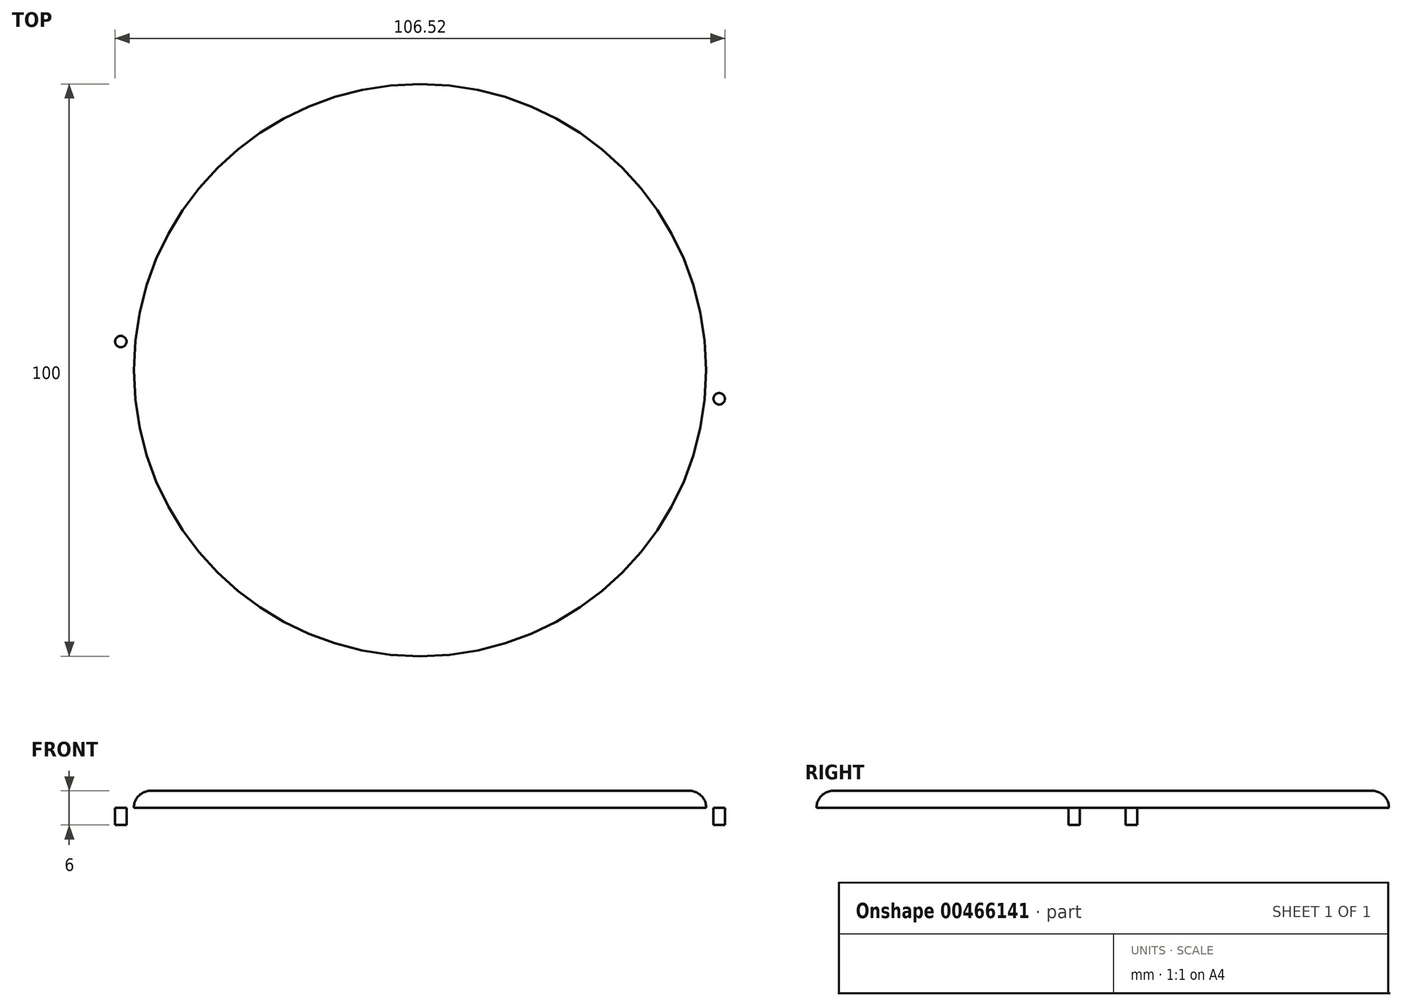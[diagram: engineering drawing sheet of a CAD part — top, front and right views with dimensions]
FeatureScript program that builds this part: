
annotation { "Feature Type Name" : "Feature", "Feature Type Description" : "" }
export const myFeature = defineFeature(function(context is Context, id is Id, definition is map)
    precondition{}
    {
        {
            var Q0;
            Q0=qCreatedBy(makeId("Top.planeOp"),FACE);
            var sketch = newSketch(context, id + "F0", { "sketchPlane" : qUnion([Q0])});
            skCircle(sketch, "E0", {"center": v(0, 0) * mm, "radius": 54 * mm});
            skSolve(sketch);
        }
        {
            var Q0;
            Q0=makeQuery(id+"F0.imprint","IMPRINT",FACE,{"disambiguationData":[TD([[makeQuery(id+"F0.imprint","IMPRINT",EDGE,{"derivedFrom":sQuery(id+"F0.wireOp",EDGE,"E0")}),1.0]])]});
            extrude(context, id + "F1", {"entities" : qUnion([Q0]), "depth" : 3 * mm});
        }
        {
            var Q0;
            Q0=makeQuery(id+"F1.opExtrude","CAP_FACE",FACE,{"disambiguationData":[OSD([sQuery(id+"F0.wireOp",EDGE,"E0")])],"isStart":false});
            var sketch = newSketch(context, id + "F2", { "sketchPlane" : qUnion([Q0])});
            skCircle(sketch, "E1", {"center": v(0, 0) * mm, "radius": 50 * mm});
            skSolve(sketch);
        }
        {
            var Q0;
            Q0=makeQuery(id+"F2.imprint","IMPRINT",FACE,{"disambiguationData":[TD([[makeQuery(id+"F2.imprint","IMPRINT",EDGE,{"derivedFrom":sQuery(id+"F2.wireOp",EDGE,"E1")}),1.0]])]});
            extrude(context, id + "F3", {"entities" : qUnion([Q0]), "offsetDistance" : 25 * mm, "depth" : 3 * mm});
        }
        {
            var Q0;
            Q0=makeQuery(id+"F3.opExtrude","CAP_FACE",FACE,{"disambiguationData":[OSD([sQuery(id+"F2.wireOp",EDGE,"E1")])],"isStart":false});
            fillet(context, id + "F4", {"entities" : qUnion([Q0]), "radius" : 3 * mm, "tangentPropagation" : true, "allowEdgeOverflow" : false});
        }
        {
            var Q0;
            Q0=makeQuery(id+"F1.opExtrude","CAP_FACE",FACE,{"disambiguationData":[OSD([sQuery(id+"F0.wireOp",EDGE,"E0")])],"isStart":true});
            var sketch = newSketch(context, id + "F5", { "sketchPlane" : qUnion([Q0])});
            skCircle(sketch, "E2", {"center": v(-52.26, 5) * mm, "radius": 1 * mm});
            skLineSegment(sketch, "E3", {"start": v(0, 0) * mm, "end": v(-54, 0) * mm, "construction": true});
            skCircle(sketch, "E4.MirrorC", {"center": v(-52.26, -5) * mm, "radius": 1 * mm});
            skLineSegment(sketch, "E5", {"start": v(0, 0) * mm, "end": v(0, 54) * mm, "construction": true});
            skCircle(sketch, "E6.MirrorC", {"center": v(52.26, 5) * mm, "radius": 1 * mm});
            skCircle(sketch, "E7.MirrorC", {"center": v(52.26, -5) * mm, "radius": 1 * mm});
            skSolve(sketch);
        }
        {
            var Q0;
            Q0=makeQuery(id+"F5.imprint","IMPRINT",FACE,{"disambiguationData":[TD([[makeQuery(id+"F5.imprint","IMPRINT",EDGE,{"derivedFrom":sQuery(id+"F5.wireOp",EDGE,"E2")}),1.0]])]});
            var Q1;
            Q1=makeQuery(id+"F5.imprint","IMPRINT",FACE,{"disambiguationData":[TD([[makeQuery(id+"F5.imprint","IMPRINT",EDGE,{"derivedFrom":sQuery(id+"F5.wireOp",EDGE,"E4.MirrorC")}),-1.0]])]});
            var Q2;
            Q2=makeQuery(id+"F5.imprint","IMPRINT",FACE,{"disambiguationData":[TD([[makeQuery(id+"F5.imprint","IMPRINT",EDGE,{"derivedFrom":sQuery(id+"F5.wireOp",EDGE,"E7.MirrorC")}),1.0]])]});
            var Q3;
            Q3=makeQuery(id+"F5.imprint","IMPRINT",FACE,{"disambiguationData":[TD([[makeQuery(id+"F5.imprint","IMPRINT",EDGE,{"derivedFrom":sQuery(id+"F5.wireOp",EDGE,"E6.MirrorC")}),-1.0]])]});
            var Q4;
            Q4=makeQuery(id+"F1.opExtrude","CAP_FACE",FACE,{"disambiguationData":[OSD([sQuery(id+"F0.wireOp",EDGE,"E0")])],"isStart":false});
            extrude(context, id + "F6", {"entities" : qUnion([Q0, Q1, Q2, Q3]), "operationType" : NewBodyOperationType.REMOVE, "endBound" : BoundingType.UP_TO_SURFACE, "oppositeDirection" : true, "endBoundEntityFace" : qUnion([Q4]), "depth" : 25 * mm});
        }
    });
